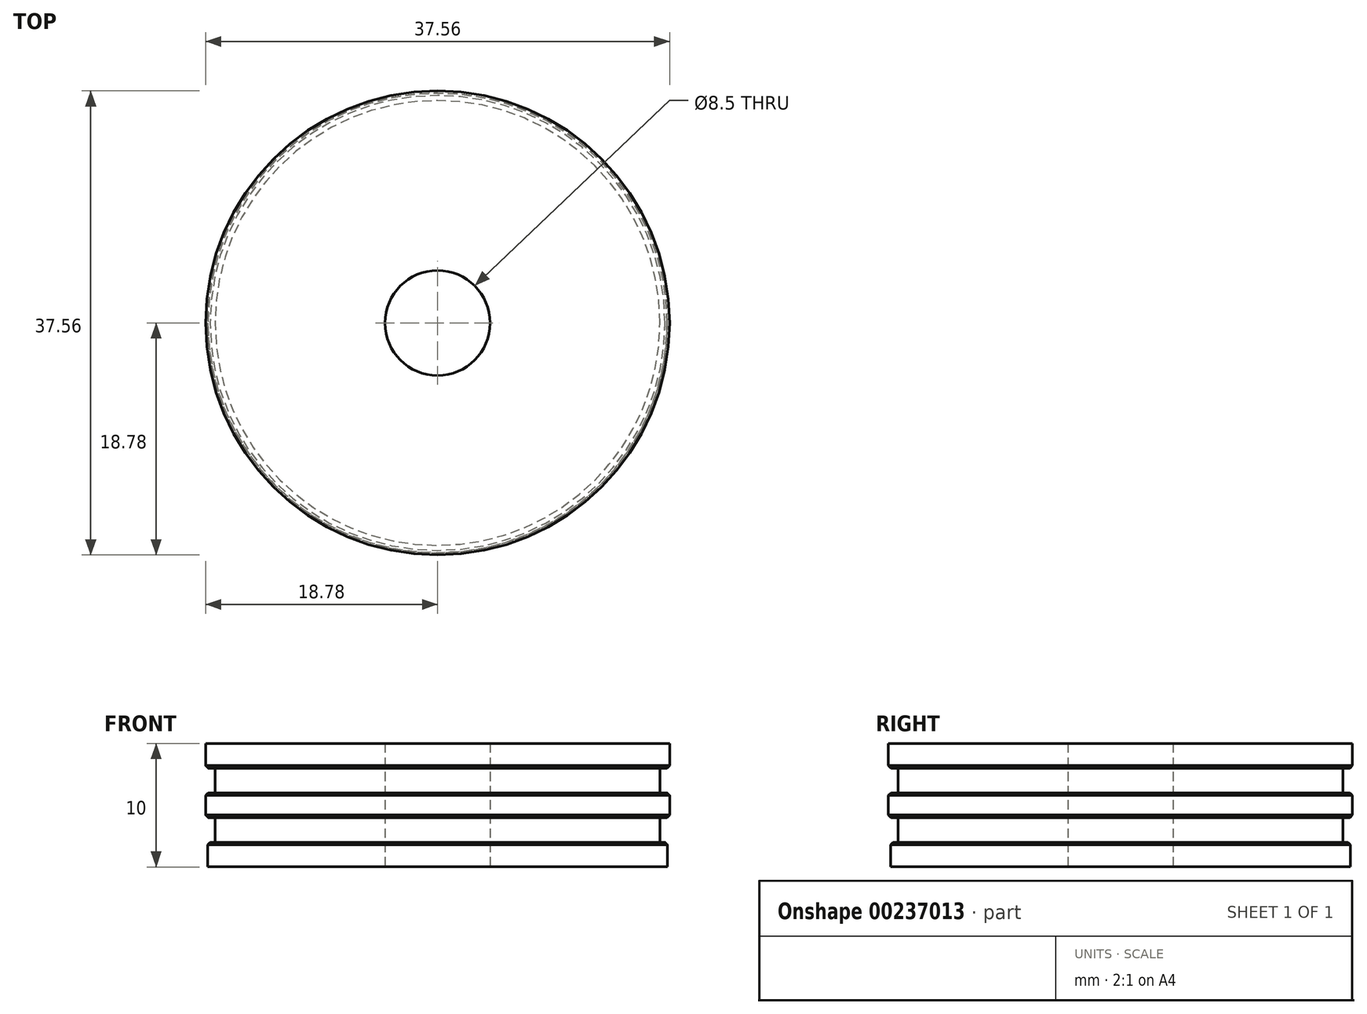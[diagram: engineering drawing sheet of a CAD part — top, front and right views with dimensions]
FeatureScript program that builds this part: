
annotation { "Feature Type Name" : "Feature", "Feature Type Description" : "" }
export const myFeature = defineFeature(function(context is Context, id is Id, definition is map)
    precondition{}
    {
        {
            var Q0;
            Q0=qCreatedBy(makeId("Front.planeOp"),FACE);
            var sketch = newSketch(context, id + "F0", { "sketchPlane" : qUnion([Q0])});
            skLineSegment(sketch, "E0", {"start": v(0, 0) * mm, "end": v(0, 10.98) * mm, "construction": true});
            skLineSegment(sketch, "E1", {"start": v(4.25, 9.46) * mm, "end": v(4.25, -0.54) * mm});
            skLineSegment(sketch, "E2", {"start": v(4.25, -0.54) * mm, "end": v(18.6, -0.54) * mm});
            skLineSegment(sketch, "E3", {"start": v(18.6, -0.54) * mm, "end": v(18.6, 1.46) * mm});
            skLineSegment(sketch, "E4", {"start": v(18.6, 1.46) * mm, "end": v(18, 1.46) * mm});
            skLineSegment(sketch, "E5", {"start": v(18, 1.46) * mm, "end": v(18, 3.46) * mm});
            skLineSegment(sketch, "E6", {"start": v(18, 3.46) * mm, "end": v(18.78, 3.46) * mm});
            skLineSegment(sketch, "E7", {"start": v(18.78, 3.46) * mm, "end": v(18.78, 5.46) * mm});
            skLineSegment(sketch, "E8", {"start": v(18.78, 5.46) * mm, "end": v(18, 5.46) * mm});
            skLineSegment(sketch, "E9", {"start": v(18, 5.46) * mm, "end": v(18, 7.46) * mm});
            skLineSegment(sketch, "E10", {"start": v(18, 7.46) * mm, "end": v(18.78, 7.46) * mm});
            skLineSegment(sketch, "E11", {"start": v(18.78, 7.46) * mm, "end": v(18.78, 9.46) * mm});
            skLineSegment(sketch, "E12", {"start": v(18.78, 9.46) * mm, "end": v(4.25, 9.46) * mm});
            skSolve(sketch);
        }
        {
            var Q0;
            Q0=makeQuery(id+"F0.imprint","IMPRINT",FACE,{"disambiguationData":[TD([[makeQuery(id+"F0.imprint","IMPRINT",EDGE,{"derivedFrom":sQuery(id+"F0.wireOp",EDGE,"E1")}),1.0]])]});
            var Q1;
            Q1=sQuery(id+"F0.wireOp",EDGE,"E0");
            revolve(context, id + "F1", {"entities" : qUnion([Q0]), "axis" : qUnion([Q1]), "revolveType" : RevolveType.FULL});
        }
        {
            var Q0;
            Q0=makeQuery(id+"F1.opRevolve","SWEPT_EDGE",EDGE,{"disambiguationData":[OSD([sQuery(id+"F0.wireOp",EDGE,"E10"),sQuery(id+"F0.wireOp",EDGE,"E11")])]});
            var Q1;
            Q1=makeQuery(id+"F1.opRevolve","SWEPT_EDGE",EDGE,{"disambiguationData":[OSD([sQuery(id+"F0.wireOp",EDGE,"E6"),sQuery(id+"F0.wireOp",EDGE,"E7")])]});
            var Q2;
            Q2=makeQuery(id+"F1.opRevolve","SWEPT_EDGE",EDGE,{"disambiguationData":[OSD([sQuery(id+"F0.wireOp",EDGE,"E3"),sQuery(id+"F0.wireOp",EDGE,"E4")])]});
            var Q3;
            Q3=makeQuery(id+"F1.opRevolve","SWEPT_EDGE",EDGE,{"disambiguationData":[OSD([sQuery(id+"F0.wireOp",EDGE,"E7"),sQuery(id+"F0.wireOp",EDGE,"E8")])]});
            chamfer(context, id + "F2", {"entities" : qUnion([Q0, Q1, Q2, Q3]), "width" : .2 * mm, "tangentPropagation" : true});
        }
    });
